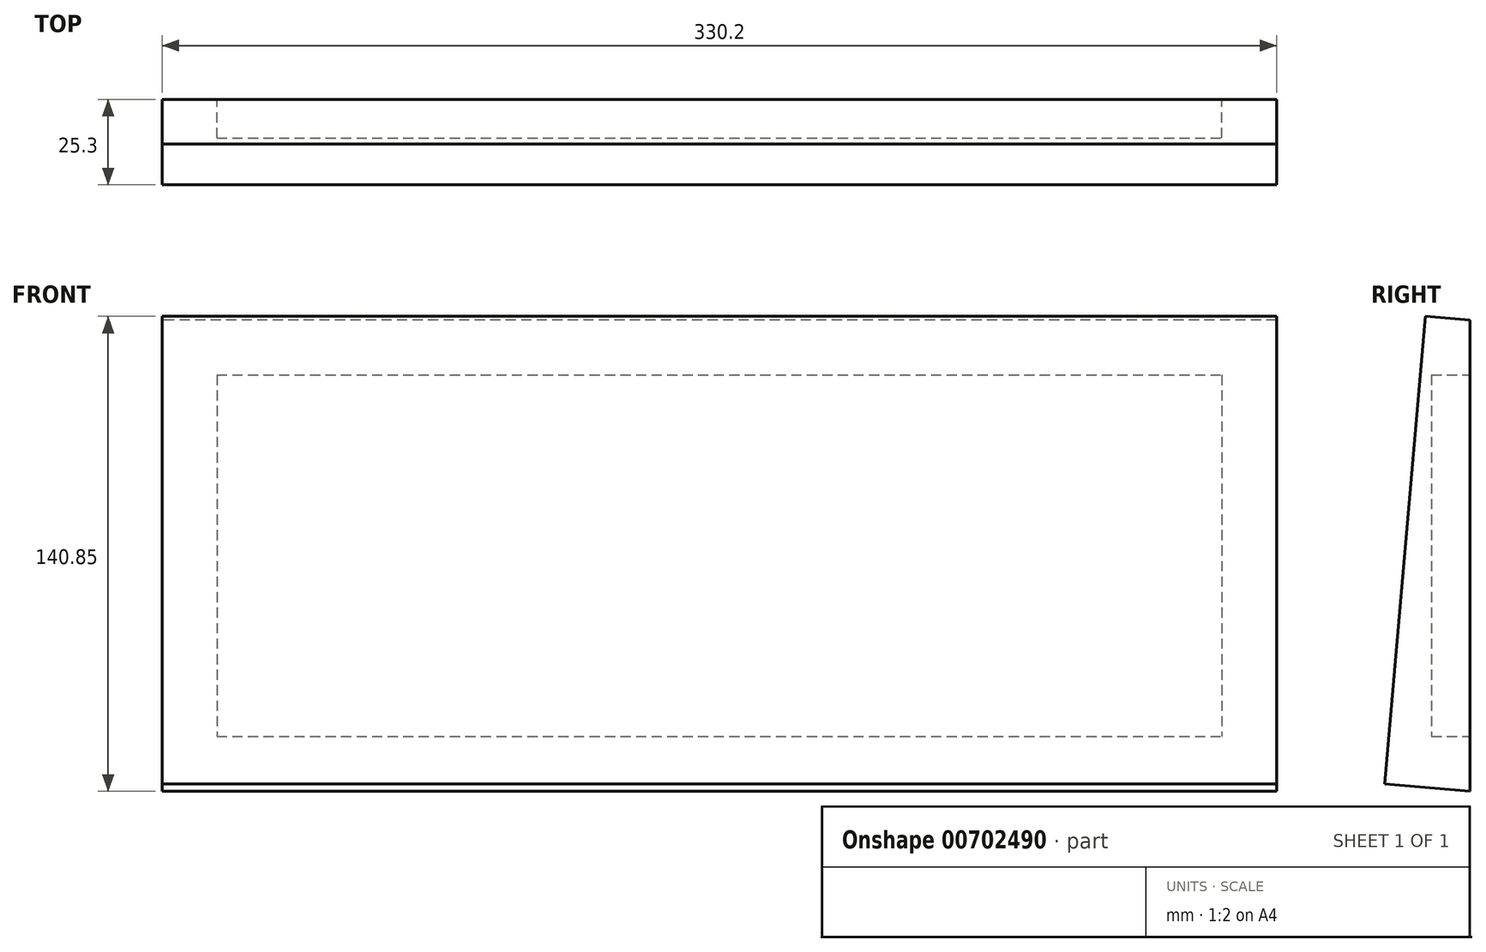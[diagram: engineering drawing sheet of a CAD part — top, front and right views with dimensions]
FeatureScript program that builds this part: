
annotation { "Feature Type Name" : "Feature", "Feature Type Description" : "" }
export const myFeature = defineFeature(function(context is Context, id is Id, definition is map)
    precondition{}
    {
        {
            var Q0;
            Q0=qCreatedBy(makeId("Front.planeOp"),FACE);
            var sketch = newSketch(context, id + "F0", { "sketchPlane" : qUnion([Q0])});
            skLineSegment(sketch, "E0.bottom", {"start": v(-143.64, 48.4) * mm, "end": v(143.64, 48.4) * mm});
            skLineSegment(sketch, "E0.top", {"start": v(-143.64, -48.4) * mm, "end": v(143.64, -48.4) * mm});
            skLineSegment(sketch, "E0.left", {"start": v(-143.64, 48.4) * mm, "end": v(-143.64, -48.4) * mm});
            skLineSegment(sketch, "E0.right", {"start": v(143.64, 48.4) * mm, "end": v(143.64, -48.4) * mm});
            skPoint(sketch, "E0.middle", {"position": v(0, 0) * mm});
            skLineSegment(sketch, "E1.bottom", {"start": v(-148.88, 53.63) * mm, "end": v(148.88, 53.63) * mm});
            skLineSegment(sketch, "E1.top", {"start": v(-148.88, -53.63) * mm, "end": v(148.88, -53.63) * mm});
            skLineSegment(sketch, "E1.left", {"start": v(-148.88, 53.63) * mm, "end": v(-148.88, -53.63) * mm});
            skLineSegment(sketch, "E1.right", {"start": v(148.88, 53.63) * mm, "end": v(148.88, -53.63) * mm});
            skLineSegment(sketch, "E2.bottom", {"start": v(-165.1, 69.85) * mm, "end": v(165.1, 69.85) * mm});
            skLineSegment(sketch, "E2.top", {"start": v(-165.1, -69.85) * mm, "end": v(165.1, -69.85) * mm});
            skLineSegment(sketch, "E2.left", {"start": v(-165.1, 69.85) * mm, "end": v(-165.1, -69.85) * mm});
            skLineSegment(sketch, "E2.right", {"start": v(165.1, 69.85) * mm, "end": v(165.1, -69.85) * mm});
            skSolve(sketch);
        }
        {
            var Q0;
            Q0=qCreatedBy(makeId("Right.planeOp"),FACE);
            var sketch = newSketch(context, id + "F1", { "sketchPlane" : qUnion([Q0])});
            skLineSegment(sketch, "E3", {"start": v(0, 0) * mm, "end": v(0, 69.85) * mm});
            skLineSegment(sketch, "E4", {"start": v(0, 0) * mm, "end": v(0, -69.85) * mm});
            skLineSegment(sketch, "E5", {"start": v(0, 69.85) * mm, "end": v(-12.13, -68.79) * mm});
            skLineSegment(sketch, "E6", {"start": v(-12.13, -68.79) * mm, "end": v(0, -69.85) * mm});
            skSolve(sketch);
        }
        {
            var Q0;
            Q0=makeQuery(id+"F1.imprint","IMPRINT",FACE,{"disambiguationData":[TD([[makeQuery(id+"F1.imprint","IMPRINT",EDGE,{"derivedFrom":sQuery(id+"F1.wireOp",EDGE,"E3")}),1.0]])]});
            extrude(context, id + "F2", {"entities" : qUnion([Q0]), "depth" : 165.1 * mm, "offsetDistance" : 25.4 * mm, "hasSecondDirection" : true, "secondDirectionOppositeDirection" : true, "secondDirectionDepth" : 165.1 * mm});
        }
        {
            var Q0;
            Q0=makeQuery(id+"F2.opExtrude","SWEPT_FACE",FACE,{"disambiguationData":[OSD([sQuery(id+"F1.wireOp",EDGE,"E5")])]});
            extrude(context, id + "F3", {"entities" : qUnion([Q0]), "operationType" : NewBodyOperationType.ADD, "depth" : 13.22 * mm, "offsetDistance" : 25.4 * mm});
        }
        {
            var Q0;
            Q0=makeQuery(id+"F0.imprint","IMPRINT",FACE,{"disambiguationData":[TD([[makeQuery(id+"F0.imprint","IMPRINT",EDGE,{"derivedFrom":sQuery(id+"F0.wireOp",EDGE,"E0.bottom")}),1.0]])]});
            var Q1;
            Q1=makeQuery(id+"F0.imprint","IMPRINT",FACE,{"disambiguationData":[TD([[makeQuery(id+"F0.imprint","IMPRINT",EDGE,{"derivedFrom":sQuery(id+"F0.wireOp",EDGE,"E0.bottom")}),-1.0]])]});
            extrude(context, id + "F4", {"entities" : qUnion([Q0, Q1]), "operationType" : NewBodyOperationType.REMOVE, "depth" : 11.43 * mm, "offsetDistance" : 25.4 * mm});
        }
    });
